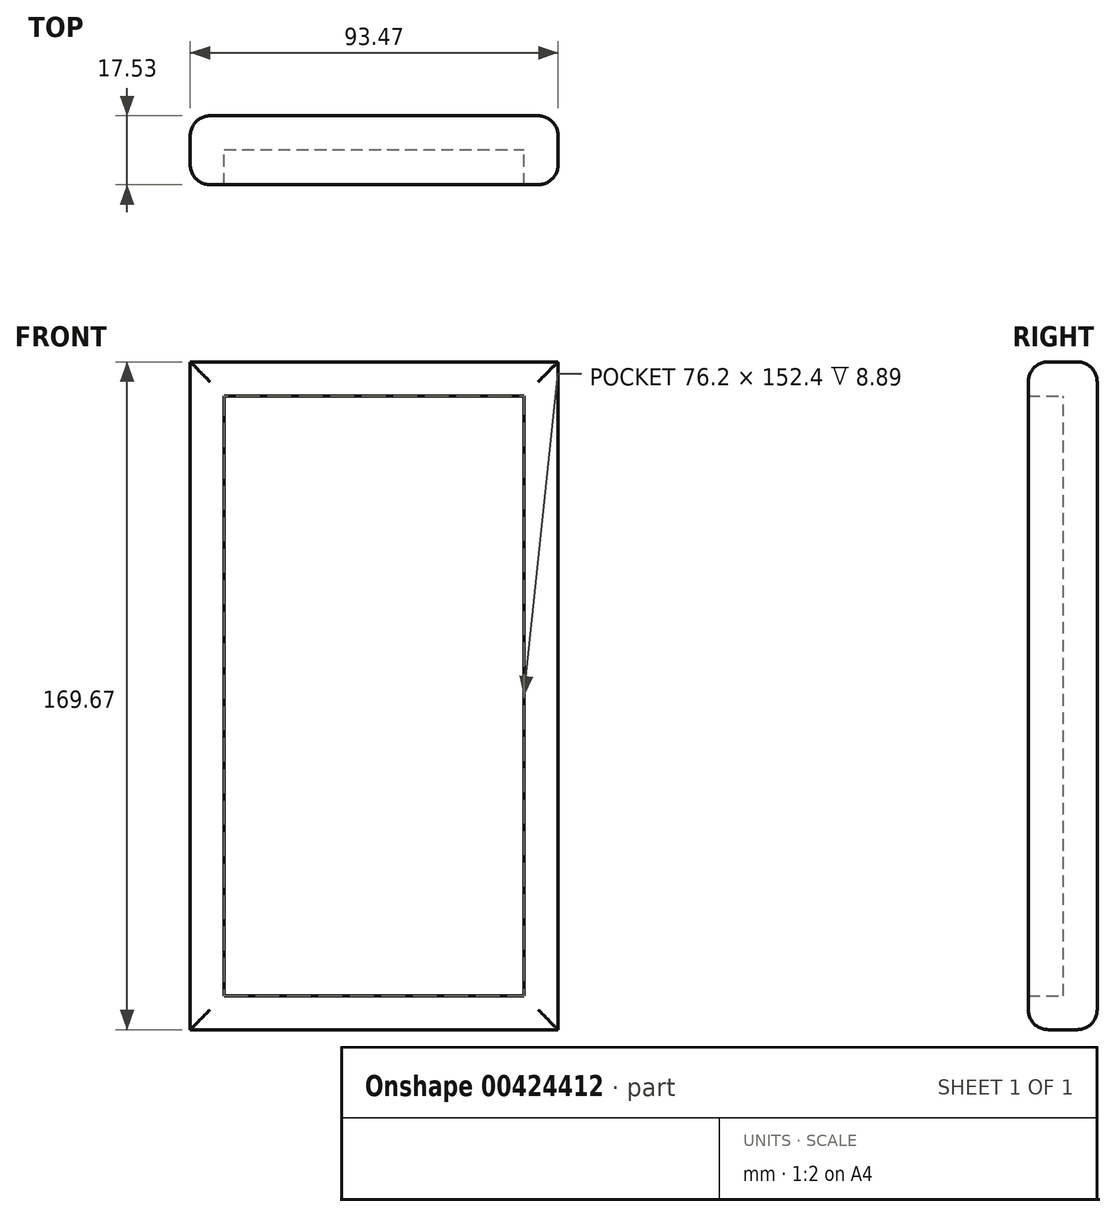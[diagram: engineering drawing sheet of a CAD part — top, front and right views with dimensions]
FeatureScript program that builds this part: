
annotation { "Feature Type Name" : "Feature", "Feature Type Description" : "" }
export const myFeature = defineFeature(function(context is Context, id is Id, definition is map)
    precondition{}
    {
        {
            var Q0;
            Q0=qCreatedBy(makeId("Front.planeOp"),FACE);
            var sketch = newSketch(context, id + "F0", { "sketchPlane" : qUnion([Q0])});
            skLineSegment(sketch, "E0.bottom", {"start": v(-36.39, -72.97) * mm, "end": v(39.81, -72.97) * mm});
            skLineSegment(sketch, "E0.top", {"start": v(-36.39, 79.43) * mm, "end": v(39.81, 79.43) * mm});
            skLineSegment(sketch, "E0.left", {"start": v(-36.39, -72.97) * mm, "end": v(-36.39, 79.43) * mm});
            skLineSegment(sketch, "E0.right", {"start": v(39.81, -72.97) * mm, "end": v(39.81, 79.43) * mm});
            skSolve(sketch);
        }
        {
            var Q0;
            Q0=makeQuery(id+"F0.imprint","IMPRINT",FACE,{"disambiguationData":[TD([[makeQuery(id+"F0.imprint","IMPRINT",EDGE,{"derivedFrom":sQuery(id+"F0.wireOp",EDGE,"E0.bottom")}),1.0]])]});
            extrude(context, id + "F1", {"entities" : qUnion([Q0]), "depth" : 8.9 * mm});
        }
        {
            var Q0;
            Q0=makeQuery(id+"F1.opExtrude","CAP_FACE",FACE,{"disambiguationData":[OSD([sQuery(id+"F0.wireOp",EDGE,"E0.bottom"),sQuery(id+"F0.wireOp",EDGE,"E0.top"),sQuery(id+"F0.wireOp",EDGE,"E0.left"),sQuery(id+"F0.wireOp",EDGE,"E0.right")])],"isStart":false});
            shell(context, id + "F2", {"entities" : qUnion([Q0]), "thickness" : 8.64 * mm, "oppositeDirection" : true});
        }
        {
            var Q0;
            Q0=makeQuery(id+"F1.opExtrude","CAP_EDGE",EDGE,{"disambiguationData":[OSD([sQuery(id+"F0.wireOp",EDGE,"E0.top")])],"isStart":false});
            var Q1;
            Q1=makeQuery(id+"F1.opExtrude","CAP_EDGE",EDGE,{"disambiguationData":[OSD([sQuery(id+"F0.wireOp",EDGE,"E0.left")])],"isStart":false});
            var Q2;
            Q2=makeQuery(id+"F1.opExtrude","CAP_EDGE",EDGE,{"disambiguationData":[OSD([sQuery(id+"F0.wireOp",EDGE,"E0.bottom")])],"isStart":false});
            var Q3;
            Q3=makeQuery(id+"F1.opExtrude","CAP_EDGE",EDGE,{"disambiguationData":[OSD([sQuery(id+"F0.wireOp",EDGE,"E0.right")])],"isStart":false});
            var Q4;
            Q4=makeQuery(id+"F1.opExtrude","CAP_EDGE",EDGE,{"disambiguationData":[OSD([sQuery(id+"F0.wireOp",EDGE,"E0.right")])],"isStart":true});
            var Q5;
            Q5=makeQuery(id+"F1.opExtrude","CAP_EDGE",EDGE,{"disambiguationData":[OSD([sQuery(id+"F0.wireOp",EDGE,"E0.top")])],"isStart":true});
            var Q6;
            Q6=makeQuery(id+"F1.opExtrude","CAP_EDGE",EDGE,{"disambiguationData":[OSD([sQuery(id+"F0.wireOp",EDGE,"E0.left")])],"isStart":true});
            var Q7;
            Q7=makeQuery(id+"F1.opExtrude","CAP_EDGE",EDGE,{"disambiguationData":[OSD([sQuery(id+"F0.wireOp",EDGE,"E0.bottom")])],"isStart":true});
            fillet(context, id + "F3", {"entities" : qUnion([Q0, Q1, Q2, Q3, Q4, Q5, Q6, Q7]), "radius" : 5.08 * mm, "tangentPropagation" : true, "allowEdgeOverflow" : false});
        }
    });
